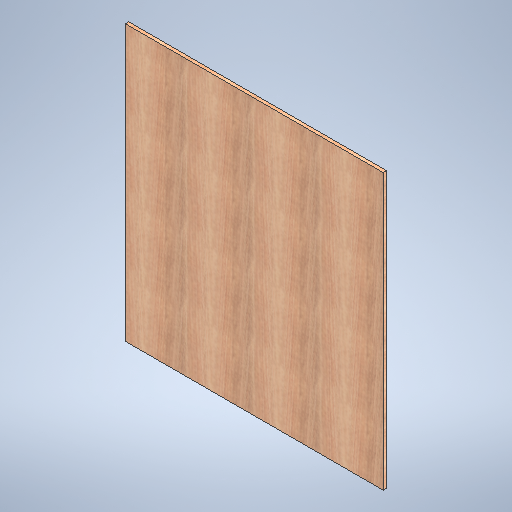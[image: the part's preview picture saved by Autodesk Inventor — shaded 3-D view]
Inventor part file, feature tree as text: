
AUTODESK INVENTOR PART (.ipt)
format: ipt  version: 2025.1 (Build 291241020, 241B)  size: 396,288 bytes
history: native  units: in
note: dims shown in document units (in); Inventor stores cm internally (conversion verified against a paired STEP export)
features: extrude x1, sketch x1
ambient origin geometry x8: Origin, YZ Plane, XZ Plane, XY Plane, X Axis, Y Axis, Z Axis, Center Point
bodies: Solid1 (feature_tree)
feature tree (2):
  extrude  "Extrusion1"  Depth=38.4375in
  sketch  "Sketch1"  dims[d2=40.979in d3=38.4375in d4=0.5in d5=0.0in]
